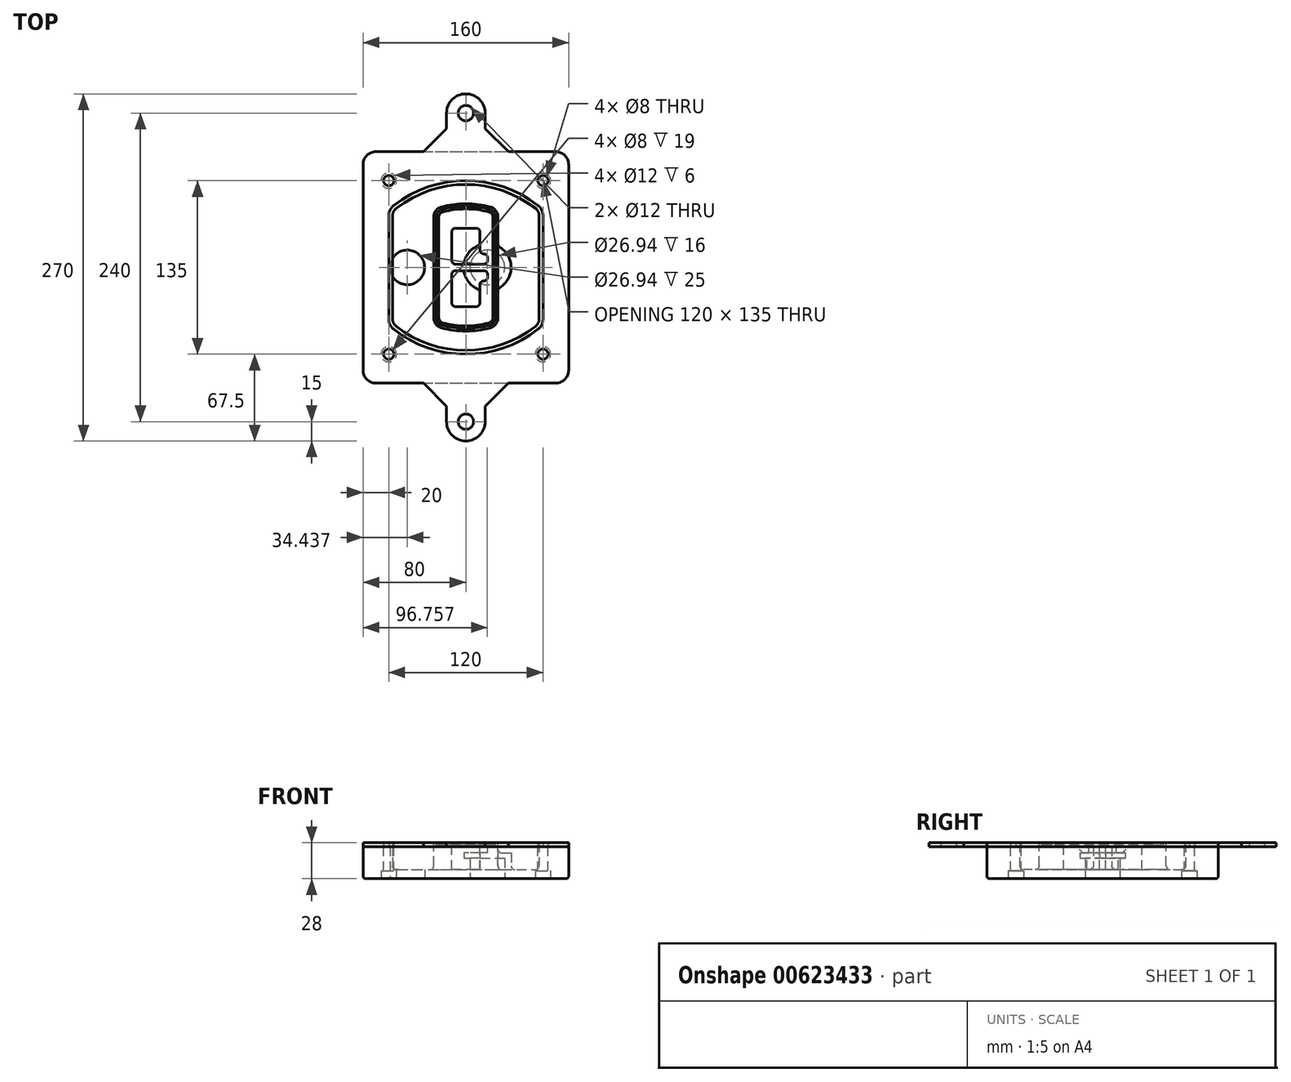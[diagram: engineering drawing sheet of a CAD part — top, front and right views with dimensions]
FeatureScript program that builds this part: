
annotation { "Feature Type Name" : "Feature", "Feature Type Description" : "" }
export const myFeature = defineFeature(function(context is Context, id is Id, definition is map)
    precondition{}
    {
        {
            var Q0;
            Q0=qCreatedBy(makeId("Top.planeOp"),FACE);
            var sketch = newSketch(context, id + "F0", { "sketchPlane" : qUnion([Q0])});
            skPoint(sketch, "E0.rect.middle", {"position": v(0, 0) * mm});
            skLineSegment(sketch, "E1.bottom", {"start": v(-70, -90) * mm, "end": v(70, -90) * mm});
            skLineSegment(sketch, "E1.top", {"start": v(-70, 90) * mm, "end": v(70, 90) * mm});
            skLineSegment(sketch, "E1.left", {"start": v(-80, -80) * mm, "end": v(-80, 80) * mm});
            skLineSegment(sketch, "E1.right", {"start": v(80, -80) * mm, "end": v(80, 80) * mm});
            skLineSegment(sketch, "E2", {"start": v(-80, 90) * mm, "end": v(80, -90) * mm, "construction": true});
            skLineSegment(sketch, "E3", {"start": v(80, 90) * mm, "end": v(-80, -90) * mm, "construction": true});
            skCircle(sketch, "E4", {"center": v(-60, 67.5) * mm, "radius": 4 * mm});
            skCircle(sketch, "E5", {"center": v(60, 67.5) * mm, "radius": 4 * mm});
            skCircle(sketch, "E6", {"center": v(60, -67.5) * mm, "radius": 4 * mm});
            skCircle(sketch, "E7", {"center": v(-60, -67.5) * mm, "radius": 4 * mm});
            skLineSegment(sketch, "E8", {"start": v(-60, 67.5) * mm, "end": v(60, 67.5) * mm, "construction": true});
            skLineSegment(sketch, "E9", {"start": v(60, 67.5) * mm, "end": v(60, -67.5) * mm, "construction": true});
            skLineSegment(sketch, "E10", {"start": v(60, -67.5) * mm, "end": v(-60, -67.5) * mm, "construction": true});
            skLineSegment(sketch, "E11", {"start": v(-60, -67.5) * mm, "end": v(-60, 67.5) * mm, "construction": true});
            skLineSegment(sketch, "E12", {"start": v(-60, 40.3) * mm, "end": v(-60, -40.3) * mm});
            skLineSegment(sketch, "E13", {"start": v(60, 40.3) * mm, "end": v(60, -40.3) * mm});
            skArc(sketch, "E14", {"start": v(56.15, 48.18) * mm, "mid": v(0, 67.5) * mm, "end": v(-56.15, 48.18) * mm});
            skArc(sketch, "E15", {"start": v(-56.15, -48.18) * mm, "mid": v(0, -67.5) * mm, "end": v(56.15, -48.18) * mm});
            skLineSegment(sketch, "E16", {"start": v(-60, 0) * mm, "end": v(60, 0) * mm, "construction": true});
            skPoint(sketch, "E17.visualSharp", {"position": v(-60, -45) * mm});
            skArc(sketch, "E17.filletArc", {"start": v(-60, -40.3) * mm, "mid": v(-58.99, -44.68) * mm, "end": v(-56.15, -48.18) * mm});
            skPoint(sketch, "E18.visualSharp", {"position": v(-60, 45) * mm});
            skArc(sketch, "E18.filletArc", {"start": v(-56.15, 48.18) * mm, "mid": v(-58.99, 44.68) * mm, "end": v(-60, 40.3) * mm});
            skPoint(sketch, "E19.visualSharp", {"position": v(60, 45) * mm});
            skArc(sketch, "E19.filletArc", {"start": v(60, 40.3) * mm, "mid": v(58.99, 44.68) * mm, "end": v(56.15, 48.18) * mm});
            skPoint(sketch, "E20.visualSharp", {"position": v(60, -45) * mm});
            skArc(sketch, "E20.filletArc", {"start": v(56.15, -48.18) * mm, "mid": v(58.99, -44.68) * mm, "end": v(60, -40.3) * mm});
            skPoint(sketch, "E21.visualSharp", {"position": v(-80, 90) * mm});
            skArc(sketch, "E21.filletArc", {"start": v(-70, 90) * mm, "mid": v(-77.07, 87.07) * mm, "end": v(-80, 80) * mm});
            skPoint(sketch, "E22.visualSharp", {"position": v(80, 90) * mm});
            skArc(sketch, "E22.filletArc", {"start": v(80, 80) * mm, "mid": v(77.07, 87.07) * mm, "end": v(70, 90) * mm});
            skPoint(sketch, "E23.visualSharp", {"position": v(80, -90) * mm});
            skArc(sketch, "E23.filletArc", {"start": v(70, -90) * mm, "mid": v(77.07, -87.07) * mm, "end": v(80, -80) * mm});
            skPoint(sketch, "E24.visualSharp", {"position": v(-80, -90) * mm});
            skArc(sketch, "E24.filletArc", {"start": v(-80, -80) * mm, "mid": v(-77.07, -87.07) * mm, "end": v(-70, -90) * mm});
            skArc(sketch, "E25.0", {"start": v(57, 40.3) * mm, "mid": v(56.3, 43.36) * mm, "end": v(54.3, 45.81) * mm});
            skLineSegment(sketch, "E25.1", {"start": v(57, 40.3) * mm, "end": v(57, -40.3) * mm});
            skArc(sketch, "E25.2", {"start": v(54.3, -45.81) * mm, "mid": v(56.3, -43.36) * mm, "end": v(57, -40.3) * mm});
            skArc(sketch, "E25.3", {"start": v(-54.3, -45.81) * mm, "mid": v(0, -64.5) * mm, "end": v(54.3, -45.81) * mm});
            skArc(sketch, "E25.4", {"start": v(-57, -40.3) * mm, "mid": v(-56.3, -43.36) * mm, "end": v(-54.3, -45.81) * mm});
            skArc(sketch, "E25.5", {"start": v(54.3, 45.81) * mm, "mid": v(0, 64.5) * mm, "end": v(-54.3, 45.81) * mm});
            skLineSegment(sketch, "E25.6", {"start": v(-57, 40.3) * mm, "end": v(-57, -40.3) * mm});
            skArc(sketch, "E25.7", {"start": v(-54.3, 45.81) * mm, "mid": v(-56.3, 43.36) * mm, "end": v(-57, 40.3) * mm});
            skArc(sketch, "E26.0", {"start": v(-58.62, 51.33) * mm, "mid": v(-62.58, 46.43) * mm, "end": v(-64, 40.3) * mm});
            skArc(sketch, "E26.1", {"start": v(58.62, 51.33) * mm, "mid": v(0, 71.5) * mm, "end": v(-58.62, 51.33) * mm});
            skArc(sketch, "E26.2", {"start": v(64, 40.3) * mm, "mid": v(62.58, 46.43) * mm, "end": v(58.62, 51.33) * mm});
            skLineSegment(sketch, "E26.3", {"start": v(64, 40.3) * mm, "end": v(64, -40.3) * mm});
            skArc(sketch, "E26.4", {"start": v(58.62, -51.33) * mm, "mid": v(62.58, -46.43) * mm, "end": v(64, -40.3) * mm});
            skLineSegment(sketch, "E26.5", {"start": v(-64, 40.3) * mm, "end": v(-64, -40.3) * mm});
            skArc(sketch, "E26.6", {"start": v(-58.62, -51.33) * mm, "mid": v(0, -71.5) * mm, "end": v(58.62, -51.33) * mm});
            skArc(sketch, "E26.7", {"start": v(-64, -40.3) * mm, "mid": v(-62.58, -46.43) * mm, "end": v(-58.62, -51.33) * mm});
            skSolve(sketch);
        }
        {
            var Q0;
            Q0=makeQuery(id+"F0.imprint","IMPRINT",FACE,{"disambiguationData":[TD([[makeQuery(id+"F0.imprint","IMPRINT",EDGE,{"derivedFrom":sQuery(id+"F0.wireOp",EDGE,"E1.bottom")}),1.0]])]});
            var Q1;
            Q1=makeQuery(id+"F0.imprint","IMPRINT",FACE,{"disambiguationData":[TD([[makeQuery(id+"F0.imprint","IMPRINT",EDGE,{"derivedFrom":sQuery(id+"F0.wireOp",EDGE,"E12")}),1.0]])]});
            var Q2;
            Q2=makeQuery(id+"F0.imprint","IMPRINT",FACE,{"disambiguationData":[TD([[makeQuery(id+"F0.imprint","IMPRINT",EDGE,{"derivedFrom":sQuery(id+"F0.wireOp",EDGE,"E25.0")}),1.0]])]});
            var Q3;
            Q3=makeQuery(id+"F0.imprint","IMPRINT",FACE,{"disambiguationData":[TD([[makeQuery(id+"F0.imprint","IMPRINT",EDGE,{"derivedFrom":sQuery(id+"F0.wireOp",EDGE,"E12")}),-1.0]])]});
            extrude(context, id + "F1", {"entities" : qUnion([Q0, Q1, Q2, Q3]), "oppositeDirection" : true, "depth" : 25 * mm});
        }
        {
            var Q0;
            Q0=makeQuery(id+"F0.imprint","IMPRINT",FACE,{"disambiguationData":[TD([[makeQuery(id+"F0.imprint","IMPRINT",EDGE,{"derivedFrom":sQuery(id+"F0.wireOp",EDGE,"E12")}),1.0]])]});
            extrude(context, id + "F2", {"entities" : qUnion([Q0]), "operationType" : NewBodyOperationType.ADD, "depth" : 3 * mm});
        }
        {
            var Q0;
            Q0=makeQuery(id+"F0.imprint","IMPRINT",FACE,{"disambiguationData":[TD([[makeQuery(id+"F0.imprint","IMPRINT",EDGE,{"derivedFrom":sQuery(id+"F0.wireOp",EDGE,"E25.0")}),1.0]])]});
            extrude(context, id + "F3", {"entities" : qUnion([Q0]), "operationType" : NewBodyOperationType.REMOVE, "oppositeDirection" : true, "depth" : 18 * mm});
        }
        {
            var Q0;
            Q0=makeQuery(id+"F2.opExtrude","CAP_FACE",FACE,{"disambiguationData":[OSD([sQuery(id+"F0.wireOp",EDGE,"E12"),sQuery(id+"F0.wireOp",EDGE,"E13"),sQuery(id+"F0.wireOp",EDGE,"E14"),sQuery(id+"F0.wireOp",EDGE,"E15"),sQuery(id+"F0.wireOp",EDGE,"E17.filletArc"),sQuery(id+"F0.wireOp",EDGE,"E18.filletArc"),sQuery(id+"F0.wireOp",EDGE,"E19.filletArc"),sQuery(id+"F0.wireOp",EDGE,"E20.filletArc"),sQuery(id+"F0.wireOp",EDGE,"E25.0"),sQuery(id+"F0.wireOp",EDGE,"E25.1"),sQuery(id+"F0.wireOp",EDGE,"E25.2"),sQuery(id+"F0.wireOp",EDGE,"E25.3"),sQuery(id+"F0.wireOp",EDGE,"E25.4"),sQuery(id+"F0.wireOp",EDGE,"E25.5"),sQuery(id+"F0.wireOp",EDGE,"E25.6"),sQuery(id+"F0.wireOp",EDGE,"E25.7")])],"isStart":false});
            var sketch = newSketch(context, id + "F4", { "sketchPlane" : qUnion([Q0])});
            skArc(sketch, "E27.0", {"start": v(-19.08, -46.97) * mm, "mid": v(0, -49.5) * mm, "end": v(19.08, -46.97) * mm});
            skArc(sketch, "E28.0", {"start": v(19.08, 46.97) * mm, "mid": v(0, 49.5) * mm, "end": v(-19.08, 46.97) * mm});
            skLineSegment(sketch, "E29", {"start": v(-25, 39.25) * mm, "end": v(-25, -39.25) * mm});
            skLineSegment(sketch, "E30", {"start": v(25, 39.25) * mm, "end": v(25, -39.25) * mm});
            skLineSegment(sketch, "E31", {"start": v(-25, 45.1) * mm, "end": v(25, 45.1) * mm, "construction": true});
            skLineSegment(sketch, "E32", {"start": v(-25, -45.1) * mm, "end": v(25, -45.1) * mm, "construction": true});
            skPoint(sketch, "E33.visualSharp", {"position": v(-25, 45.1) * mm});
            skArc(sketch, "E33.filletArc", {"start": v(-19.08, 46.97) * mm, "mid": v(-23.35, 44.11) * mm, "end": v(-25, 39.25) * mm});
            skPoint(sketch, "E34.visualSharp", {"position": v(25, 45.1) * mm});
            skArc(sketch, "E34.filletArc", {"start": v(25, 39.25) * mm, "mid": v(23.35, 44.11) * mm, "end": v(19.08, 46.97) * mm});
            skPoint(sketch, "E35.visualSharp", {"position": v(25, -45.1) * mm});
            skArc(sketch, "E35.filletArc", {"start": v(19.08, -46.97) * mm, "mid": v(23.35, -44.11) * mm, "end": v(25, -39.25) * mm});
            skPoint(sketch, "E36.visualSharp", {"position": v(-25, -45.1) * mm});
            skArc(sketch, "E36.filletArc", {"start": v(-25, -39.25) * mm, "mid": v(-23.35, -44.11) * mm, "end": v(-19.08, -46.97) * mm});
            skArc(sketch, "E37.0", {"start": v(54.3, 45.81) * mm, "mid": v(0, 64.5) * mm, "end": v(-54.3, 45.81) * mm});
            skArc(sketch, "E37.1", {"start": v(-54.3, 45.81) * mm, "mid": v(-56.3, 43.36) * mm, "end": v(-57, 40.3) * mm});
            skLineSegment(sketch, "E37.2", {"start": v(-57, 40.3) * mm, "end": v(-57, -40.3) * mm});
            skArc(sketch, "E37.3", {"start": v(-57, -40.3) * mm, "mid": v(-56.3, -43.36) * mm, "end": v(-54.3, -45.81) * mm});
            skArc(sketch, "E37.4", {"start": v(-54.3, -45.81) * mm, "mid": v(0, -64.5) * mm, "end": v(54.3, -45.81) * mm});
            skArc(sketch, "E37.5", {"start": v(54.3, -45.81) * mm, "mid": v(56.3, -43.36) * mm, "end": v(57, -40.3) * mm});
            skLineSegment(sketch, "E37.6", {"start": v(57, 40.3) * mm, "end": v(57, -40.3) * mm});
            skArc(sketch, "E37.7", {"start": v(57, 40.3) * mm, "mid": v(56.3, 43.36) * mm, "end": v(54.3, 45.81) * mm});
            skLineSegment(sketch, "E38.0", {"start": v(23, 39.25) * mm, "end": v(23, -39.25) * mm});
            skArc(sketch, "E38.1", {"start": v(18.56, -45.04) * mm, "mid": v(21.76, -42.9) * mm, "end": v(23, -39.25) * mm});
            skArc(sketch, "E38.2", {"start": v(-18.56, -45.04) * mm, "mid": v(0, -47.5) * mm, "end": v(18.56, -45.04) * mm});
            skArc(sketch, "E38.3", {"start": v(-23, -39.25) * mm, "mid": v(-21.76, -42.9) * mm, "end": v(-18.56, -45.04) * mm});
            skLineSegment(sketch, "E38.4", {"start": v(-23, 39.25) * mm, "end": v(-23, -39.25) * mm});
            skArc(sketch, "E38.5", {"start": v(23, 39.25) * mm, "mid": v(21.76, 42.9) * mm, "end": v(18.56, 45.04) * mm});
            skArc(sketch, "E38.6", {"start": v(-18.56, 45.04) * mm, "mid": v(-21.76, 42.9) * mm, "end": v(-23, 39.25) * mm});
            skArc(sketch, "E38.7", {"start": v(18.56, 45.04) * mm, "mid": v(0, 47.5) * mm, "end": v(-18.56, 45.04) * mm});
            skArc(sketch, "E39.0", {"start": v(21, 39.25) * mm, "mid": v(20.18, 41.68) * mm, "end": v(18.04, 43.1) * mm});
            skLineSegment(sketch, "E39.1", {"start": v(21, 39.25) * mm, "end": v(21, -39.25) * mm});
            skArc(sketch, "E39.2", {"start": v(18.04, -43.1) * mm, "mid": v(20.18, -41.68) * mm, "end": v(21, -39.25) * mm});
            skArc(sketch, "E39.3", {"start": v(-18.04, -43.1) * mm, "mid": v(0, -45.5) * mm, "end": v(18.04, -43.1) * mm});
            skArc(sketch, "E39.4", {"start": v(-21, -39.25) * mm, "mid": v(-20.18, -41.68) * mm, "end": v(-18.04, -43.1) * mm});
            skArc(sketch, "E39.5", {"start": v(18.04, 43.1) * mm, "mid": v(0, 45.5) * mm, "end": v(-18.04, 43.1) * mm});
            skLineSegment(sketch, "E39.6", {"start": v(-21, 39.25) * mm, "end": v(-21, -39.25) * mm});
            skArc(sketch, "E39.7", {"start": v(-18.04, 43.1) * mm, "mid": v(-20.18, 41.68) * mm, "end": v(-21, 39.25) * mm});
            skLineSegment(sketch, "E40", {"start": v(-25, 0) * mm, "end": v(25, 0) * mm, "construction": true});
            skLineSegment(sketch, "E41", {"start": v(-11, 5.5) * mm, "end": v(-11, 27.5) * mm});
            skLineSegment(sketch, "E42", {"start": v(-8, 30.5) * mm, "end": v(8, 30.5) * mm});
            skLineSegment(sketch, "E43", {"start": v(11, 27.5) * mm, "end": v(11, 13.5) * mm});
            skLineSegment(sketch, "E44", {"start": v(14, 10.5) * mm, "end": v(14, 10.5) * mm});
            skLineSegment(sketch, "E45", {"start": v(17, 7.5) * mm, "end": v(17, 5.5) * mm});
            skLineSegment(sketch, "E46", {"start": v(14, 2.5) * mm, "end": v(-8, 2.5) * mm});
            skPoint(sketch, "E47.visualSharp", {"position": v(-11, 30.5) * mm});
            skArc(sketch, "E47.filletArc", {"start": v(-8, 30.5) * mm, "mid": v(-10.12, 29.62) * mm, "end": v(-11, 27.5) * mm});
            skPoint(sketch, "E48.visualSharp", {"position": v(11, 30.5) * mm});
            skArc(sketch, "E48.filletArc", {"start": v(11, 27.5) * mm, "mid": v(10.12, 29.62) * mm, "end": v(8, 30.5) * mm});
            skPoint(sketch, "E49.visualSharp", {"position": v(11, 10.5) * mm});
            skArc(sketch, "E49.filletArc", {"start": v(11, 13.5) * mm, "mid": v(11.88, 11.38) * mm, "end": v(14, 10.5) * mm});
            skPoint(sketch, "E50.visualSharp", {"position": v(17, 10.5) * mm});
            skArc(sketch, "E50.filletArc", {"start": v(17, 7.5) * mm, "mid": v(16.12, 9.62) * mm, "end": v(14, 10.5) * mm});
            skPoint(sketch, "E51.visualSharp", {"position": v(17, 2.5) * mm});
            skArc(sketch, "E51.filletArc", {"start": v(14, 2.5) * mm, "mid": v(16.12, 3.38) * mm, "end": v(17, 5.5) * mm});
            skPoint(sketch, "E52.visualSharp", {"position": v(-11, 2.5) * mm});
            skArc(sketch, "E52.filletArc", {"start": v(-11, 5.5) * mm, "mid": v(-10.12, 3.38) * mm, "end": v(-8, 2.5) * mm});
            skLineSegment(sketch, "E53.0.MirrorCS", {"start": v(14, -2.5) * mm, "end": v(-8, -2.5) * mm});
            skArc(sketch, "E54.0.MirrorCS", {"start": v(-11, -5.5) * mm, "mid": v(-10.12, -3.38) * mm, "end": v(-8, -2.5) * mm});
            skLineSegment(sketch, "E55.0.MirrorCS", {"start": v(-11, -5.5) * mm, "end": v(-11, -27.5) * mm});
            skArc(sketch, "E56.0.MirrorCS", {"start": v(-8, -30.5) * mm, "mid": v(-10.12, -29.62) * mm, "end": v(-11, -27.5) * mm});
            skLineSegment(sketch, "E57.0.MirrorCS", {"start": v(-8, -30.5) * mm, "end": v(8, -30.5) * mm});
            skArc(sketch, "E58.0.MirrorCS", {"start": v(11, -27.5) * mm, "mid": v(10.12, -29.62) * mm, "end": v(8, -30.5) * mm});
            skLineSegment(sketch, "E59.0.MirrorCS", {"start": v(11, -27.5) * mm, "end": v(11, -13.5) * mm});
            skArc(sketch, "E60.0.MirrorCS", {"start": v(11, -13.5) * mm, "mid": v(11.88, -11.38) * mm, "end": v(14, -10.5) * mm});
            skArc(sketch, "E61.0.MirrorCS", {"start": v(17, -7.5) * mm, "mid": v(16.12, -9.62) * mm, "end": v(14, -10.5) * mm});
            skLineSegment(sketch, "E62.0.MirrorCS", {"start": v(17, -7.5) * mm, "end": v(17, -5.5) * mm});
            skArc(sketch, "E63.0.MirrorCS", {"start": v(14, -2.5) * mm, "mid": v(16.12, -3.38) * mm, "end": v(17, -5.5) * mm});
            skSolve(sketch);
        }
        {
            var Q0;
            Q0=makeQuery(id+"F4.imprint","IMPRINT",FACE,{"disambiguationData":[TD([[makeQuery(id+"F4.imprint","IMPRINT",EDGE,{"derivedFrom":sQuery(id+"F4.wireOp",EDGE,"E27.0")}),1.0]])]});
            var Q1;
            Q1=makeQuery(id+"F4.imprint","IMPRINT",FACE,{"disambiguationData":[TD([[makeQuery(id+"F4.imprint","IMPRINT",EDGE,{"derivedFrom":sQuery(id+"F4.wireOp",EDGE,"E38.0")}),-1.0]])]});
            var Q2;
            Q2=makeQuery(id+"F4.imprint","IMPRINT",FACE,{"disambiguationData":[TD([[makeQuery(id+"F4.imprint","IMPRINT",EDGE,{"derivedFrom":sQuery(id+"F4.wireOp",EDGE,"E39.0")}),1.0]])]});
            extrude(context, id + "F5", {"entities" : qUnion([Q0, Q1, Q2]), "operationType" : NewBodyOperationType.ADD, "endBound" : BoundingType.UP_TO_NEXT, "oppositeDirection" : true, "depth" : 25 * mm});
        }
        {
            var Q0;
            Q0=makeQuery(id+"F4.imprint","IMPRINT",FACE,{"disambiguationData":[TD([[makeQuery(id+"F4.imprint","IMPRINT",EDGE,{"derivedFrom":sQuery(id+"F4.wireOp",EDGE,"E38.0")}),-1.0]])]});
            extrude(context, id + "F6", {"entities" : qUnion([Q0]), "operationType" : NewBodyOperationType.REMOVE, "oppositeDirection" : true, "depth" : 2 * mm});
        }
        {
            var Q0;
            Q0=makeQuery(id+"F1.opExtrude","CAP_FACE",FACE,{"disambiguationData":[OSD([sQuery(id+"F0.wireOp",EDGE,"E1.bottom"),sQuery(id+"F0.wireOp",EDGE,"E1.top"),sQuery(id+"F0.wireOp",EDGE,"E1.left"),sQuery(id+"F0.wireOp",EDGE,"E1.right"),sQuery(id+"F0.wireOp",EDGE,"E4"),sQuery(id+"F0.wireOp",EDGE,"E5"),sQuery(id+"F0.wireOp",EDGE,"E6"),sQuery(id+"F0.wireOp",EDGE,"E7"),sQuery(id+"F0.wireOp",EDGE,"E21.filletArc"),sQuery(id+"F0.wireOp",EDGE,"E22.filletArc"),sQuery(id+"F0.wireOp",EDGE,"E23.filletArc"),sQuery(id+"F0.wireOp",EDGE,"E24.filletArc")])],"isStart":false});
            var sketch = newSketch(context, id + "F7", { "sketchPlane" : qUnion([Q0])});
            skCircle(sketch, "E64", {"center": v(16.76, 0) * mm, "radius": 13.47 * mm});
            skCircle(sketch, "E65", {"center": v(-45.56, 0) * mm, "radius": 13.47 * mm});
            skLineSegment(sketch, "E66", {"start": v(80, 0) * mm, "end": v(-80, 0) * mm});
            skCircle(sketch, "E67", {"center": v(16.76, 0) * mm, "radius": 18.47 * mm});
            skCircle(sketch, "E68", {"center": v(60, -67.5) * mm, "radius": 6 * mm});
            skCircle(sketch, "E69", {"center": v(-60, -67.5) * mm, "radius": 6 * mm});
            skCircle(sketch, "E70", {"center": v(-60, 67.5) * mm, "radius": 6 * mm});
            skCircle(sketch, "E71", {"center": v(60, 67.5) * mm, "radius": 6 * mm});
            skSolve(sketch);
        }
        {
            var Q0;
            {var subQ1=sQuery(id+"F7.wireOp",EDGE,"E66");var subQ4=sQuery(id+"F7.wireOp",EDGE,"E64");var subQ6=makeQuery(id+"F7.imprint","INTERSECT",VERTEX,{"disambiguationData":[OD(0.0)],"derivedFrom":[subQ4,subQ1]});Q0=makeQuery(id+"F7.imprint","IMPRINT",FACE,{"disambiguationData":[TD([[makeQuery(id+"F7.imprint","IMPRINT",EDGE,{"disambiguationData":[TD([[subQ6,-1.0]])],"derivedFrom":subQ4}),-1.0]])]});}
            var Q1;
            {var subQ0=sQuery(id+"F7.wireOp",EDGE,"E66");var subQ1=sQuery(id+"F7.wireOp",EDGE,"E64");var subQ3=makeQuery(id+"F7.imprint","INTERSECT",VERTEX,{"disambiguationData":[OD(0.0)],"derivedFrom":[subQ1,subQ0]});Q1=makeQuery(id+"F7.imprint","IMPRINT",FACE,{"disambiguationData":[TD([[makeQuery(id+"F7.imprint","IMPRINT",EDGE,{"disambiguationData":[TD([[subQ3,-1.0]])],"derivedFrom":subQ1}),1.0]])]});}
            var Q2;
            {var subQ0=sQuery(id+"F7.wireOp",EDGE,"E66");var subQ1=sQuery(id+"F7.wireOp",EDGE,"E64");var subQ3=makeQuery(id+"F7.imprint","INTERSECT",VERTEX,{"disambiguationData":[OD(0.0)],"derivedFrom":[subQ1,subQ0]});Q2=makeQuery(id+"F7.imprint","IMPRINT",FACE,{"disambiguationData":[TD([[makeQuery(id+"F7.imprint","IMPRINT",EDGE,{"disambiguationData":[TD([[subQ3,1.0]])],"derivedFrom":subQ1}),1.0]])]});}
            var Q3;
            {var subQ1=sQuery(id+"F7.wireOp",EDGE,"E66");var subQ4=sQuery(id+"F7.wireOp",EDGE,"E64");var subQ6=makeQuery(id+"F7.imprint","INTERSECT",VERTEX,{"disambiguationData":[OD(0.0)],"derivedFrom":[subQ4,subQ1]});Q3=makeQuery(id+"F7.imprint","IMPRINT",FACE,{"disambiguationData":[TD([[makeQuery(id+"F7.imprint","IMPRINT",EDGE,{"disambiguationData":[TD([[subQ6,1.0]])],"derivedFrom":subQ4}),-1.0]])]});}
            extrude(context, id + "F8", {"entities" : qUnion([Q0, Q1, Q2, Q3]), "operationType" : NewBodyOperationType.ADD, "oppositeDirection" : true, "depth" : 20 * mm});
        }
        {
            var Q0;
            {var subQ0=sQuery(id+"F7.wireOp",EDGE,"E66");var subQ1=sQuery(id+"F7.wireOp",EDGE,"E64");var subQ3=makeQuery(id+"F7.imprint","INTERSECT",VERTEX,{"disambiguationData":[OD(0.0)],"derivedFrom":[subQ1,subQ0]});Q0=makeQuery(id+"F7.imprint","IMPRINT",FACE,{"disambiguationData":[TD([[makeQuery(id+"F7.imprint","IMPRINT",EDGE,{"disambiguationData":[TD([[subQ3,-1.0]])],"derivedFrom":subQ1}),1.0]])]});}
            var Q1;
            {var subQ0=sQuery(id+"F7.wireOp",EDGE,"E66");var subQ1=sQuery(id+"F7.wireOp",EDGE,"E64");var subQ3=makeQuery(id+"F7.imprint","INTERSECT",VERTEX,{"disambiguationData":[OD(0.0)],"derivedFrom":[subQ1,subQ0]});Q1=makeQuery(id+"F7.imprint","IMPRINT",FACE,{"disambiguationData":[TD([[makeQuery(id+"F7.imprint","IMPRINT",EDGE,{"disambiguationData":[TD([[subQ3,1.0]])],"derivedFrom":subQ1}),1.0]])]});}
            extrude(context, id + "F9", {"entities" : qUnion([Q0, Q1]), "operationType" : NewBodyOperationType.REMOVE, "oppositeDirection" : true, "depth" : 16 * mm});
        }
        {
            var Q0;
            {var subQ0=sQuery(id+"F7.wireOp",EDGE,"E66");var subQ1=sQuery(id+"F7.wireOp",EDGE,"E65");var subQ3=makeQuery(id+"F7.imprint","INTERSECT",VERTEX,{"disambiguationData":[OD(0.0)],"derivedFrom":[subQ1,subQ0]});Q0=makeQuery(id+"F7.imprint","IMPRINT",FACE,{"disambiguationData":[TD([[makeQuery(id+"F7.imprint","IMPRINT",EDGE,{"disambiguationData":[TD([[subQ3,-1.0]])],"derivedFrom":subQ1}),1.0]])]});}
            var Q1;
            {var subQ0=sQuery(id+"F7.wireOp",EDGE,"E66");var subQ1=sQuery(id+"F7.wireOp",EDGE,"E65");var subQ3=makeQuery(id+"F7.imprint","INTERSECT",VERTEX,{"disambiguationData":[OD(0.0)],"derivedFrom":[subQ1,subQ0]});Q1=makeQuery(id+"F7.imprint","IMPRINT",FACE,{"disambiguationData":[TD([[makeQuery(id+"F7.imprint","IMPRINT",EDGE,{"disambiguationData":[TD([[subQ3,1.0]])],"derivedFrom":subQ1}),1.0]])]});}
            extrude(context, id + "F10", {"entities" : qUnion([Q0, Q1]), "operationType" : NewBodyOperationType.REMOVE, "oppositeDirection" : true, "depth" : 25 * mm});
        }
        {
            var Q0;
            Q0=makeQuery(id+"F7.imprint","IMPRINT",FACE,{"disambiguationData":[TD([[makeQuery(id+"F7.imprint","IMPRINT",EDGE,{"derivedFrom":sQuery(id+"F7.wireOp",EDGE,"E68")}),1.0]])]});
            var Q1;
            Q1=makeQuery(id+"F7.imprint","IMPRINT",FACE,{"disambiguationData":[TD([[makeQuery(id+"F7.imprint","IMPRINT",EDGE,{"derivedFrom":makeQuery(id+"F1.opExtrude","CAP_EDGE",EDGE,{"disambiguationData":[OSD([sQuery(id+"F0.wireOp",EDGE,"E5")])],"isStart":false})}),-1.0]])]});
            var Q2;
            Q2=makeQuery(id+"F7.imprint","IMPRINT",FACE,{"disambiguationData":[TD([[makeQuery(id+"F7.imprint","IMPRINT",EDGE,{"derivedFrom":sQuery(id+"F7.wireOp",EDGE,"E69")}),1.0]])]});
            var Q3;
            Q3=makeQuery(id+"F7.imprint","IMPRINT",FACE,{"disambiguationData":[TD([[makeQuery(id+"F7.imprint","IMPRINT",EDGE,{"derivedFrom":makeQuery(id+"F1.opExtrude","CAP_EDGE",EDGE,{"disambiguationData":[OSD([sQuery(id+"F0.wireOp",EDGE,"E4")])],"isStart":false})}),-1.0]])]});
            var Q4;
            Q4=makeQuery(id+"F7.imprint","IMPRINT",FACE,{"disambiguationData":[TD([[makeQuery(id+"F7.imprint","IMPRINT",EDGE,{"derivedFrom":sQuery(id+"F7.wireOp",EDGE,"E70")}),1.0]])]});
            var Q5;
            Q5=makeQuery(id+"F7.imprint","IMPRINT",FACE,{"disambiguationData":[TD([[makeQuery(id+"F7.imprint","IMPRINT",EDGE,{"derivedFrom":makeQuery(id+"F1.opExtrude","CAP_EDGE",EDGE,{"disambiguationData":[OSD([sQuery(id+"F0.wireOp",EDGE,"E7")])],"isStart":false})}),-1.0]])]});
            var Q6;
            Q6=makeQuery(id+"F7.imprint","IMPRINT",FACE,{"disambiguationData":[TD([[makeQuery(id+"F7.imprint","IMPRINT",EDGE,{"derivedFrom":sQuery(id+"F7.wireOp",EDGE,"E71")}),1.0]])]});
            var Q7;
            Q7=makeQuery(id+"F7.imprint","IMPRINT",FACE,{"disambiguationData":[TD([[makeQuery(id+"F7.imprint","IMPRINT",EDGE,{"derivedFrom":makeQuery(id+"F1.opExtrude","CAP_EDGE",EDGE,{"disambiguationData":[OSD([sQuery(id+"F0.wireOp",EDGE,"E6")])],"isStart":false})}),-1.0]])]});
            extrude(context, id + "F11", {"entities" : qUnion([Q0, Q1, Q2, Q3, Q4, Q5, Q6, Q7]), "operationType" : NewBodyOperationType.REMOVE, "oppositeDirection" : true, "depth" : 6 * mm});
        }
        {
            var Q0;
            Q0=makeQuery(id+"F9.boolean.opBoolean","COPY",FACE,{"derivedFrom":makeQuery(id+"F9.opExtrude","CAP_FACE",FACE,{"disambiguationData":[OSD([sQuery(id+"F7.wireOp",EDGE,"E64")])],"isStart":false})});
            var sketch = newSketch(context, id + "F12", { "sketchPlane" : qUnion([Q0])});
            skArc(sketch, "E72.0", {"start": v(11, 17.55) * mm, "mid": v(2.57, 11.82) * mm, "end": v(-1.54, 2.5) * mm});
            skArc(sketch, "E72.1", {"start": v(-1.54, -2.5) * mm, "mid": v(2.57, -11.82) * mm, "end": v(11, -17.55) * mm});
            skLineSegment(sketch, "E73", {"start": v(-1.54, -2.5) * mm, "end": v(14, -2.5) * mm});
            skLineSegment(sketch, "E74.0", {"start": v(14, 2.5) * mm, "end": v(-1.54, 2.5) * mm});
            skArc(sketch, "E74.1", {"start": v(14, 2.5) * mm, "mid": v(16.12, 3.38) * mm, "end": v(17, 5.5) * mm});
            skLineSegment(sketch, "E74.2", {"start": v(17, 7.5) * mm, "end": v(17, 5.5) * mm});
            skArc(sketch, "E74.3", {"start": v(17, 7.5) * mm, "mid": v(16.12, 9.62) * mm, "end": v(14, 10.5) * mm});
            skArc(sketch, "E74.4", {"start": v(11, 13.5) * mm, "mid": v(11.88, 11.38) * mm, "end": v(14, 10.5) * mm});
            skLineSegment(sketch, "E74.5", {"start": v(11, 17.55) * mm, "end": v(11, 13.5) * mm});
            skLineSegment(sketch, "E74.7", {"start": v(14, -2.5) * mm, "end": v(-1.54, -2.5) * mm});
            skArc(sketch, "E74.8", {"start": v(14, -2.5) * mm, "mid": v(16.12, -3.38) * mm, "end": v(17, -5.5) * mm});
            skLineSegment(sketch, "E74.9", {"start": v(17, -7.5) * mm, "end": v(17, -5.5) * mm});
            skArc(sketch, "E74.10", {"start": v(17, -7.5) * mm, "mid": v(16.12, -9.62) * mm, "end": v(14, -10.5) * mm});
            skArc(sketch, "E74.11", {"start": v(11, -13.5) * mm, "mid": v(11.88, -11.38) * mm, "end": v(14, -10.5) * mm});
            skLineSegment(sketch, "E74.12", {"start": v(11, -17.55) * mm, "end": v(11, -13.5) * mm});
            skPoint(sketch, "E75.orphan", {"position": v(11, -27.5) * mm});
            skPoint(sketch, "E76.orphan", {"position": v(-8, -2.5) * mm});
            skPoint(sketch, "E77.orphan", {"position": v(-8, 2.5) * mm});
            skPoint(sketch, "E78.orphan", {"position": v(11, 27.5) * mm});
            skSolve(sketch);
        }
        {
            var Q0;
            {var subQ7=sQuery(id+"F12.wireOp",EDGE,"E72.0");var subQ14=sQuery(id+"F12.wireOp",EDGE,"E72.1");var subQ16=sQuery(id+"F12.wireOp",EDGE,"E74.1");var subQ18=sQuery(id+"F12.wireOp",EDGE,"E74.8");Q0=qUnion([makeQuery(id+"F12.imprint","IMPRINT",FACE,{"disambiguationData":[TD([[makeQuery(id+"F12.imprint","IMPRINT",EDGE,{"derivedFrom":subQ7}),1.0]])]}),makeQuery(id+"F12.imprint","IMPRINT",FACE,{"disambiguationData":[TD([[makeQuery(id+"F12.imprint","IMPRINT",EDGE,{"derivedFrom":subQ14}),1.0]])]}),makeQuery(id+"F12.imprint","IMPRINT",FACE,{"disambiguationData":[TD([[makeQuery(id+"F12.imprint","IMPRINT",EDGE,{"derivedFrom":subQ16}),1.0]])]}),makeQuery(id+"F12.imprint","IMPRINT",FACE,{"disambiguationData":[TD([[makeQuery(id+"F12.imprint","IMPRINT",EDGE,{"derivedFrom":subQ18}),-1.0]])]})]);}
            var Q1;
            Q1=makeQuery(id+"F5.boolean.opBoolean","SPLIT",FACE,{"disambiguationData":[TD([makeQuery(id+"F5.opExtrude","SWEPT_FACE",FACE,{"disambiguationData":[OSD([sQuery(id+"F4.wireOp",EDGE,"E41")])]})])],"derivedFrom":makeQuery(id+"F3.boolean.opBoolean","COPY",FACE,{"derivedFrom":makeQuery(id+"F3.opExtrude","CAP_FACE",FACE,{"disambiguationData":[OSD([sQuery(id+"F0.wireOp",EDGE,"E25.0"),sQuery(id+"F0.wireOp",EDGE,"E25.1"),sQuery(id+"F0.wireOp",EDGE,"E25.2"),sQuery(id+"F0.wireOp",EDGE,"E25.3"),sQuery(id+"F0.wireOp",EDGE,"E25.4"),sQuery(id+"F0.wireOp",EDGE,"E25.5"),sQuery(id+"F0.wireOp",EDGE,"E25.6"),sQuery(id+"F0.wireOp",EDGE,"E25.7")])],"isStart":false})})});
            extrude(context, id + "F13", {"entities" : qUnion([Q0]), "operationType" : NewBodyOperationType.REMOVE, "endBound" : BoundingType.UP_TO_SURFACE, "endBoundEntityFace" : qUnion([Q1]), "depth" : 25 * mm});
        }
        {
            var Q0;
            Q0=makeQuery(id+"F3.boolean.opBoolean","COPY",EDGE,{"derivedFrom":makeQuery(id+"F3.opExtrude","CAP_EDGE",EDGE,{"disambiguationData":[OSD([sQuery(id+"F0.wireOp",EDGE,"E25.6")])],"isStart":false})});
            var Q1;
            Q1=makeQuery(id+"F8.boolean.opBoolean","INTERSECT",EDGE,{"derivedFrom":[makeQuery(id+"F5.opExtrude","SWEPT_FACE",FACE,{"disambiguationData":[OSD([sQuery(id+"F4.wireOp",EDGE,"E30")])]}),makeQuery(id+"F8.opExtrude","CAP_FACE",FACE,{"disambiguationData":[OSD([sQuery(id+"F7.wireOp",EDGE,"E67")])],"isStart":false})]});
            var Q2;
            Q2=makeQuery(id+"F8.boolean.opBoolean","INTERSECT",EDGE,{"disambiguationData":[OD(1.0)],"derivedFrom":[makeQuery(id+"F5.opExtrude","SWEPT_FACE",FACE,{"disambiguationData":[OSD([sQuery(id+"F4.wireOp",EDGE,"E30")])]}),makeQuery(id+"F8.opExtrude","SWEPT_FACE",FACE,{"disambiguationData":[OSD([sQuery(id+"F7.wireOp",EDGE,"E67")])]})]});
            var Q3;
            {var subQ0=sQuery(id+"F4.wireOp",EDGE,"E30");Q3=makeQuery(id+"F8.boolean.opBoolean","SPLIT",EDGE,{"disambiguationData":[TD([makeQuery(id+"F5.opExtrude","SWEPT_FACE",FACE,{"disambiguationData":[OSD([sQuery(id+"F4.wireOp",EDGE,"E35.filletArc")])]})])],"derivedFrom":makeQuery(id+"F5.opExtrude","CAP_EDGE",EDGE,{"disambiguationData":[OSD([subQ0])],"isStart":false})});}
            var Q4;
            {var subQ0=sQuery(id+"F0.wireOp",EDGE,"E25.7");var subQ1=sQuery(id+"F0.wireOp",EDGE,"E25.1");var subQ2=sQuery(id+"F0.wireOp",EDGE,"E25.6");var subQ3=sQuery(id+"F0.wireOp",EDGE,"E25.5");var subQ4=sQuery(id+"F0.wireOp",EDGE,"E25.4");var subQ5=sQuery(id+"F0.wireOp",EDGE,"E25.0");var subQ6=sQuery(id+"F0.wireOp",EDGE,"E25.2");var subQ7=sQuery(id+"F0.wireOp",EDGE,"E25.3");Q4=makeQuery(id+"F8.boolean.opBoolean","INTERSECT",EDGE,{"derivedFrom":[makeQuery(id+"F5.boolean.opBoolean","SPLIT",FACE,{"disambiguationData":[TD([makeQuery(id+"F2.opExtrude","SWEPT_FACE",FACE,{"disambiguationData":[OSD([subQ5])]})])],"derivedFrom":makeQuery(id+"F3.boolean.opBoolean","COPY",FACE,{"derivedFrom":makeQuery(id+"F3.opExtrude","CAP_FACE",FACE,{"disambiguationData":[OSD([subQ5,subQ1,subQ6,subQ7,subQ4,subQ3,subQ2,subQ0])],"isStart":false})})}),makeQuery(id+"F8.opExtrude","SWEPT_FACE",FACE,{"disambiguationData":[OSD([sQuery(id+"F7.wireOp",EDGE,"E67")])]})]});}
            var Q5;
            Q5=makeQuery(id+"F8.boolean.opBoolean","INTERSECT",EDGE,{"disambiguationData":[OD(0.0)],"derivedFrom":[makeQuery(id+"F5.opExtrude","SWEPT_FACE",FACE,{"disambiguationData":[OSD([sQuery(id+"F4.wireOp",EDGE,"E30")])]}),makeQuery(id+"F8.opExtrude","SWEPT_FACE",FACE,{"disambiguationData":[OSD([sQuery(id+"F7.wireOp",EDGE,"E67")])]})]});
            fillet(context, id + "F14", {"entities" : qUnion([Q0, Q1, Q2, Q3, Q4, Q5]), "radius" : 3 * mm, "tangentPropagation" : true, "allowEdgeOverflow" : false});
        }
        {
            var Q0;
            Q0=makeQuery(id+"F1.opExtrude","CAP_EDGE",EDGE,{"disambiguationData":[OSD([sQuery(id+"F0.wireOp",EDGE,"E1.bottom")])],"isStart":false});
            fillet(context, id + "F15", {"entities" : qUnion([Q0]), "radius" : 2 * mm, "tangentPropagation" : true, "allowEdgeOverflow" : false});
        }
        {
            var Q0;
            {var subQ0=sQuery(id+"F0.wireOp",EDGE,"E21.filletArc");var subQ1=sQuery(id+"F0.wireOp",EDGE,"E7");var subQ2=sQuery(id+"F0.wireOp",EDGE,"E6");var subQ3=sQuery(id+"F0.wireOp",EDGE,"E5");var subQ4=sQuery(id+"F0.wireOp",EDGE,"E4");var subQ5=sQuery(id+"F0.wireOp",EDGE,"E22.filletArc");var subQ6=sQuery(id+"F0.wireOp",EDGE,"E1.bottom");var subQ7=sQuery(id+"F0.wireOp",EDGE,"E1.right");var subQ8=sQuery(id+"F0.wireOp",EDGE,"E1.top");var subQ9=sQuery(id+"F0.wireOp",EDGE,"E1.left");var subQ10=sQuery(id+"F0.wireOp",EDGE,"E23.filletArc");var subQ11=sQuery(id+"F0.wireOp",EDGE,"E24.filletArc");Q0=makeQuery(id+"F2.boolean.opBoolean","SPLIT",FACE,{"disambiguationData":[TD([makeQuery(id+"F1.opExtrude","SWEPT_FACE",FACE,{"disambiguationData":[OSD([subQ6])]})])],"derivedFrom":makeQuery(id+"F1.opExtrude","CAP_FACE",FACE,{"disambiguationData":[OSD([subQ6,subQ8,subQ9,subQ7,subQ4,subQ3,subQ2,subQ1,subQ0,subQ5,subQ10,subQ11])],"isStart":true})});}
            var sketch = newSketch(context, id + "F16", { "sketchPlane" : qUnion([Q0])});
            skLineSegment(sketch, "E79.0", {"start": v(-80, -80) * mm, "end": v(-80, 80) * mm});
            skArc(sketch, "E79.1", {"start": v(-80, -80) * mm, "mid": v(-77.07, -87.07) * mm, "end": v(-70, -90) * mm});
            skLineSegment(sketch, "E79.2", {"start": v(-70, -90) * mm, "end": v(70, -90) * mm});
            skArc(sketch, "E79.3", {"start": v(70, -90) * mm, "mid": v(77.07, -87.07) * mm, "end": v(80, -80) * mm});
            skLineSegment(sketch, "E79.4", {"start": v(80, -80) * mm, "end": v(80, 80) * mm});
            skArc(sketch, "E79.5", {"start": v(80, 80) * mm, "mid": v(77.07, 87.07) * mm, "end": v(70, 90) * mm});
            skLineSegment(sketch, "E79.6", {"start": v(-70, 90) * mm, "end": v(70, 90) * mm});
            skArc(sketch, "E79.7", {"start": v(-70, 90) * mm, "mid": v(-77.07, 87.07) * mm, "end": v(-80, 80) * mm});
            skCircle(sketch, "E79.8", {"center": v(-60, 67.5) * mm, "radius": 4 * mm});
            skCircle(sketch, "E79.9", {"center": v(-60, -67.5) * mm, "radius": 4 * mm});
            skCircle(sketch, "E79.10", {"center": v(60, -67.5) * mm, "radius": 4 * mm});
            skCircle(sketch, "E79.11", {"center": v(60, 67.5) * mm, "radius": 4 * mm});
            skArc(sketch, "E79.12", {"start": v(56.15, 48.18) * mm, "mid": v(0, 67.5) * mm, "end": v(-56.15, 48.18) * mm});
            skArc(sketch, "E79.13", {"start": v(-56.15, 48.18) * mm, "mid": v(-58.99, 44.68) * mm, "end": v(-60, 40.3) * mm});
            skLineSegment(sketch, "E79.14", {"start": v(-60, 40.3) * mm, "end": v(-60, -40.3) * mm});
            skArc(sketch, "E79.15", {"start": v(-60, -40.3) * mm, "mid": v(-58.99, -44.68) * mm, "end": v(-56.15, -48.18) * mm});
            skArc(sketch, "E79.16", {"start": v(-56.15, -48.18) * mm, "mid": v(0, -67.5) * mm, "end": v(56.15, -48.18) * mm});
            skArc(sketch, "E79.17", {"start": v(56.15, -48.18) * mm, "mid": v(58.99, -44.68) * mm, "end": v(60, -40.3) * mm});
            skLineSegment(sketch, "E79.18", {"start": v(60, 40.3) * mm, "end": v(60, -40.3) * mm});
            skArc(sketch, "E79.19", {"start": v(60, 40.3) * mm, "mid": v(58.99, 44.68) * mm, "end": v(56.15, 48.18) * mm});
            skLineSegment(sketch, "E80", {"start": v(0, 90) * mm, "end": v(0, 120) * mm, "construction": true});
            skCircle(sketch, "E81", {"center": v(0, 120) * mm, "radius": 6 * mm});
            skArc(sketch, "E82", {"start": v(15, 120) * mm, "mid": v(0, 135) * mm, "end": v(-15, 120) * mm});
            skLineSegment(sketch, "E83", {"start": v(-15, 120) * mm, "end": v(-15, 108) * mm});
            skLineSegment(sketch, "E84", {"start": v(-15, 108) * mm, "end": v(-33, 90) * mm});
            skLineSegment(sketch, "E85.MirrorCS", {"start": v(15, 108) * mm, "end": v(33, 90) * mm});
            skLineSegment(sketch, "E86.MirrorCS", {"start": v(15, 120) * mm, "end": v(15, 108) * mm});
            skLineSegment(sketch, "E87", {"start": v(-80, 0) * mm, "end": v(80, 0) * mm, "construction": true});
            skLineSegment(sketch, "E88.MirrorCS", {"start": v(-15, -120) * mm, "end": v(-15, -108) * mm});
            skLineSegment(sketch, "E89.MirrorCS", {"start": v(15, -120) * mm, "end": v(15, -108) * mm});
            skCircle(sketch, "E90.MirrorC", {"center": v(0, -120) * mm, "radius": 6 * mm});
            skLineSegment(sketch, "E91.MirrorCS", {"start": v(15, -108) * mm, "end": v(33, -90) * mm});
            skArc(sketch, "E92.MirrorCS", {"start": v(15, -120) * mm, "mid": v(0, -135) * mm, "end": v(-15, -120) * mm});
            skLineSegment(sketch, "E93.MirrorCS", {"start": v(0, -90) * mm, "end": v(0, -120) * mm, "construction": true});
            skArc(sketch, "E94.MirrorCS", {"start": v(56.15, -48.18) * mm, "mid": v(0, -67.5) * mm, "end": v(-56.15, -48.18) * mm});
            skLineSegment(sketch, "E95.MirrorCS", {"start": v(-15, -108) * mm, "end": v(-33, -90) * mm});
            skSolve(sketch);
        }
        {
            var Q0;
            Q0=makeQuery(id+"F16.imprint","IMPRINT",FACE,{"disambiguationData":[TD([[makeQuery(id+"F16.imprint","IMPRINT",EDGE,{"derivedFrom":sQuery(id+"F16.wireOp",EDGE,"E79.0")}),-1.0]])]});
            var Q1;
            Q1=makeQuery(id+"F16.imprint","IMPRINT",FACE,{"disambiguationData":[TD([[makeQuery(id+"F16.imprint","IMPRINT",EDGE,{"derivedFrom":sQuery(id+"F16.wireOp",EDGE,"E81")}),-1.0]])]});
            var Q2;
            Q2=makeQuery(id+"F16.imprint","IMPRINT",FACE,{"disambiguationData":[TD([[makeQuery(id+"F16.imprint","IMPRINT",EDGE,{"derivedFrom":sQuery(id+"F16.wireOp",EDGE,"E88.MirrorCS")}),-1.0]])]});
            var Q3;
            Q3=makeQuery(id+"F2.opExtrude","CAP_FACE",FACE,{"disambiguationData":[OSD([sQuery(id+"F0.wireOp",EDGE,"E12"),sQuery(id+"F0.wireOp",EDGE,"E13"),sQuery(id+"F0.wireOp",EDGE,"E14"),sQuery(id+"F0.wireOp",EDGE,"E15"),sQuery(id+"F0.wireOp",EDGE,"E17.filletArc"),sQuery(id+"F0.wireOp",EDGE,"E18.filletArc"),sQuery(id+"F0.wireOp",EDGE,"E19.filletArc"),sQuery(id+"F0.wireOp",EDGE,"E20.filletArc"),sQuery(id+"F0.wireOp",EDGE,"E25.0"),sQuery(id+"F0.wireOp",EDGE,"E25.1"),sQuery(id+"F0.wireOp",EDGE,"E25.2"),sQuery(id+"F0.wireOp",EDGE,"E25.3"),sQuery(id+"F0.wireOp",EDGE,"E25.4"),sQuery(id+"F0.wireOp",EDGE,"E25.5"),sQuery(id+"F0.wireOp",EDGE,"E25.6"),sQuery(id+"F0.wireOp",EDGE,"E25.7")])],"isStart":false});
            extrude(context, id + "F17", {"entities" : qUnion([Q0, Q1, Q2]), "endBound" : BoundingType.UP_TO_SURFACE, "depth" : 25 * mm, "endBoundEntityFace" : qUnion([Q3]), "offsetDistance" : 25 * mm});
        }
    });
